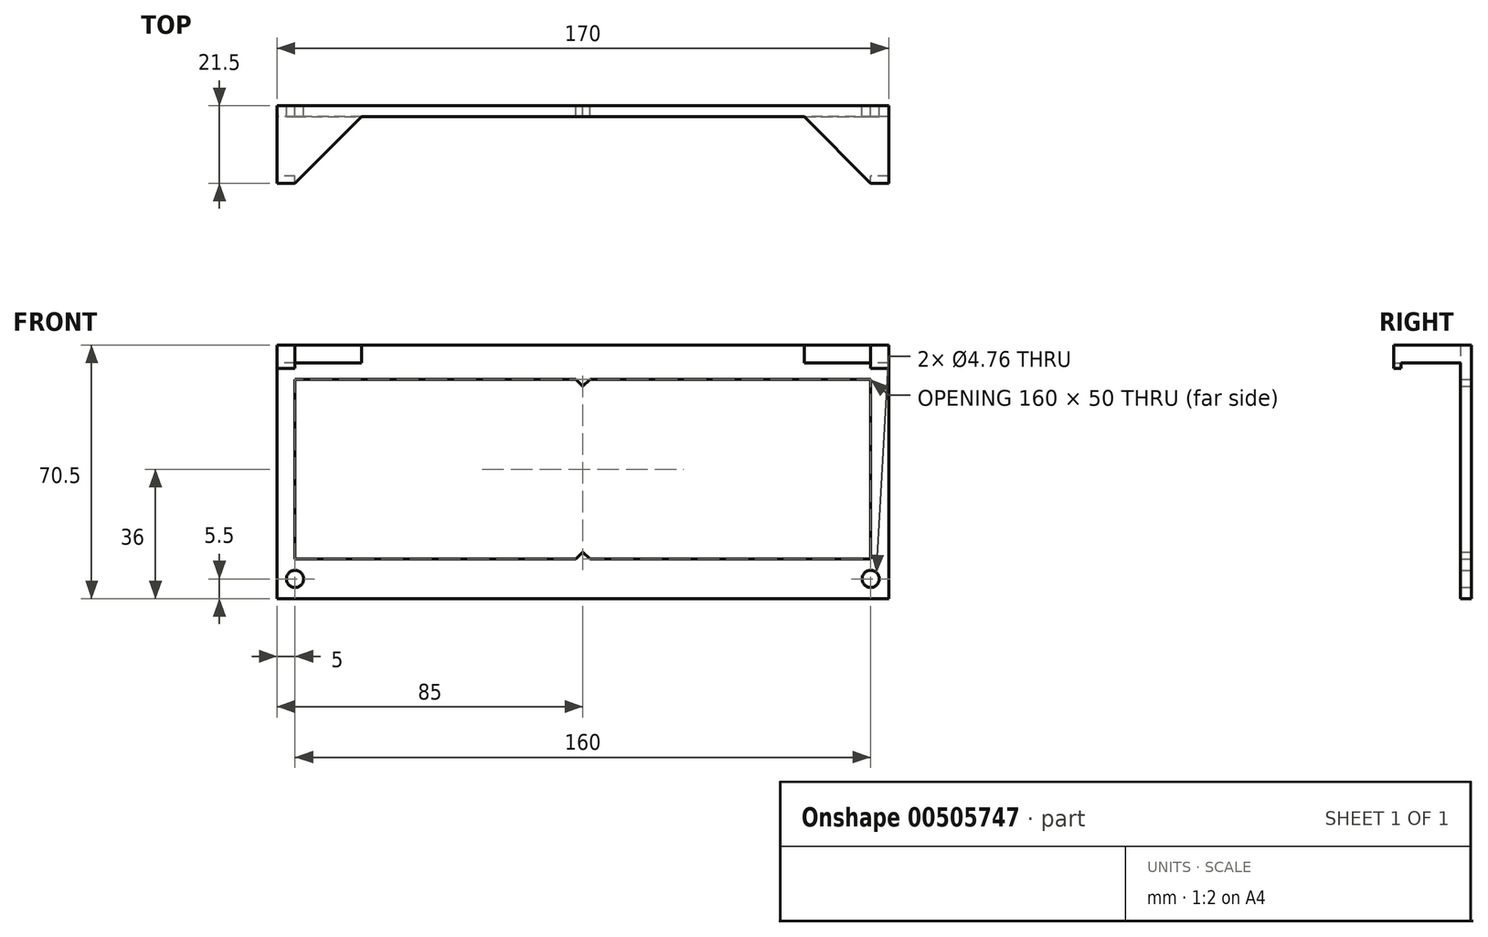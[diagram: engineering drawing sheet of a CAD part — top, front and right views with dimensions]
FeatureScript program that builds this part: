
annotation { "Feature Type Name" : "Feature", "Feature Type Description" : "" }
export const myFeature = defineFeature(function(context is Context, id is Id, definition is map)
    precondition{}
    {
        {
            var Q0;
            Q0=qCreatedBy(makeId("Front.planeOp"),FACE);
            var sketch = newSketch(context, id + "F0", { "sketchPlane" : qUnion([Q0])});
            skLineSegment(sketch, "E0.bottom", {"start": v(0, 0) * mm, "end": v(170, 0) * mm});
            skLineSegment(sketch, "E0.top", {"start": v(0, -67.5) * mm, "end": v(170, -67.5) * mm});
            skLineSegment(sketch, "E0.left", {"start": v(0, 0) * mm, "end": v(0, -67.5) * mm});
            skLineSegment(sketch, "E0.right", {"start": v(170, 0) * mm, "end": v(170, -67.5) * mm});
            skCircle(sketch, "E1", {"center": v(5, -62) * mm, "radius": 2.38 * mm});
            skCircle(sketch, "E2", {"center": v(165, -62) * mm, "radius": 2.38 * mm});
            skLineSegment(sketch, "E3", {"start": v(0, -1.5) * mm, "end": v(170, -1.5) * mm});
            skLineSegment(sketch, "E4.left", {"start": v(5, -6.5) * mm, "end": v(5, -56.5) * mm});
            skLineSegment(sketch, "E4.right", {"start": v(165, -6.5) * mm, "end": v(165, -56.5) * mm});
            skLineSegment(sketch, "E5", {"start": v(5, -6.5) * mm, "end": v(83, -6.5) * mm});
            skLineSegment(sketch, "E6", {"start": v(83, -6.5) * mm, "end": v(85, -8.5) * mm});
            skLineSegment(sketch, "E7", {"start": v(85, -8.5) * mm, "end": v(87, -6.5) * mm});
            skLineSegment(sketch, "E8", {"start": v(87, -6.5) * mm, "end": v(165, -6.5) * mm});
            skLineSegment(sketch, "E9", {"start": v(5, -56.5) * mm, "end": v(83, -56.5) * mm});
            skLineSegment(sketch, "E10", {"start": v(83, -56.5) * mm, "end": v(85, -54.5) * mm});
            skLineSegment(sketch, "E11", {"start": v(85, -54.5) * mm, "end": v(87, -56.5) * mm});
            skLineSegment(sketch, "E12", {"start": v(87, -56.5) * mm, "end": v(165, -56.5) * mm});
            skSolve(sketch);
        }
        {
            var Q0;
            {var subQ1=sQuery(id+"F0.wireOp",EDGE,"E0.top");Q0=makeQuery(id+"F0.imprint","IMPRINT",FACE,{"disambiguationData":[TD([[makeQuery(id+"F0.imprint","IMPRINT",EDGE,{"derivedFrom":subQ1}),1.0]])]});}
            extrude(context, id + "F1", {"entities" : qUnion([Q0]), "depth" : 3 * mm});
        }
        {
            var Q0;
            {var subQ0=sQuery(id+"F0.wireOp",EDGE,"E0.bottom");Q0=makeQuery(id+"F0.imprint","IMPRINT",FACE,{"disambiguationData":[TD([[makeQuery(id+"F0.imprint","IMPRINT",EDGE,{"derivedFrom":subQ0}),-1.0]])]});}
            extrude(context, id + "F2", {"entities" : qUnion([Q0]), "operationType" : NewBodyOperationType.ADD, "depth" : 21.5 * mm});
        }
        {
            var Q0;
            Q0=makeQuery(id+"F2.opExtrude","SWEPT_FACE",FACE,{"disambiguationData":[OSD([sQuery(id+"F0.wireOp",EDGE,"E3")])]});
            var sketch = newSketch(context, id + "F3", { "sketchPlane" : qUnion([Q0])});
            skLineSegment(sketch, "E13.bottom", {"start": v(0, 21.5) * mm, "end": v(170, 21.5) * mm});
            skLineSegment(sketch, "E13.top", {"start": v(0, 19.5) * mm, "end": v(170, 19.5) * mm});
            skLineSegment(sketch, "E13.left", {"start": v(0, 21.5) * mm, "end": v(0, 19.5) * mm});
            skLineSegment(sketch, "E13.right", {"start": v(170, 21.5) * mm, "end": v(170, 19.5) * mm});
            skSolve(sketch);
        }
        {
            var Q0;
            Q0=makeQuery(id+"F3.imprint","IMPRINT",FACE,{"disambiguationData":[TD([[makeQuery(id+"F3.imprint","IMPRINT",EDGE,{"derivedFrom":sQuery(id+"F3.wireOp",EDGE,"E13.bottom")}),-1.0]])]});
            extrude(context, id + "F4", {"entities" : qUnion([Q0]), "operationType" : NewBodyOperationType.ADD, "depth" : 2 * mm});
        }
        {
            var Q0;
            Q0=makeQuery(id+"F4.opExtrude","CAP_FACE",FACE,{"disambiguationData":[OSD([sQuery(id+"F3.wireOp",EDGE,"E13.bottom"),sQuery(id+"F3.wireOp",EDGE,"E13.top"),sQuery(id+"F3.wireOp",EDGE,"E13.left"),sQuery(id+"F3.wireOp",EDGE,"E13.right")])],"isStart":false});
            var sketch = newSketch(context, id + "F5", { "sketchPlane" : qUnion([Q0])});
            skLineSegment(sketch, "E14.bottom", {"start": v(5, 21.5) * mm, "end": v(165, 21.5) * mm});
            skLineSegment(sketch, "E14.top", {"start": v(5, 3) * mm, "end": v(165, 3) * mm});
            skLineSegment(sketch, "E14.left", {"start": v(5, 21.5) * mm, "end": v(5, 3) * mm});
            skLineSegment(sketch, "E14.right", {"start": v(165, 21.5) * mm, "end": v(165, 3) * mm});
            skSolve(sketch);
        }
        {
            var Q0;
            Q0 = qSketchRegion(id + "F5", true);
            extrude(context, id + "F6", {"entities" : qUnion([Q0]), "operationType" : NewBodyOperationType.REMOVE, "endBound" : BoundingType.THROUGH_ALL, "oppositeDirection" : true, "depth" : 25 * mm});
        }
        {
            var Q0;
            Q0=makeQuery(id+"F2.opExtrude","SWEPT_FACE",FACE,{"disambiguationData":[OSD([sQuery(id+"F0.wireOp",EDGE,"E0.bottom")])]});
            var sketch = newSketch(context, id + "F7", { "sketchPlane" : qUnion([Q0])});
            skLineSegment(sketch, "E15", {"start": v(0, -21.5) * mm, "end": v(0, 0) * mm});
            skLineSegment(sketch, "E16", {"start": v(0, 0) * mm, "end": v(170, 0) * mm});
            skLineSegment(sketch, "E17", {"start": v(170, 0) * mm, "end": v(170, -21.5) * mm});
            skLineSegment(sketch, "E18", {"start": v(170, -21.5) * mm, "end": v(165, -21.5) * mm});
            skLineSegment(sketch, "E19", {"start": v(165, -21.5) * mm, "end": v(146.5, -3) * mm});
            skLineSegment(sketch, "E20", {"start": v(146.5, -3) * mm, "end": v(23.5, -3) * mm});
            skLineSegment(sketch, "E21", {"start": v(23.5, -3) * mm, "end": v(5, -21.5) * mm});
            skLineSegment(sketch, "E22", {"start": v(5, -21.5) * mm, "end": v(0, -21.5) * mm});
            skSolve(sketch);
        }
        {
            var Q0;
            Q0 = qSketchRegion(id + "F7", true);
            extrude(context, id + "F8", {"entities" : qUnion([Q0]), "operationType" : NewBodyOperationType.ADD, "depth" : 3 * mm, "hasSecondDirection" : true, "secondDirectionOppositeDirection" : true, "secondDirectionDepth" : 2 * mm});
        }
    });
